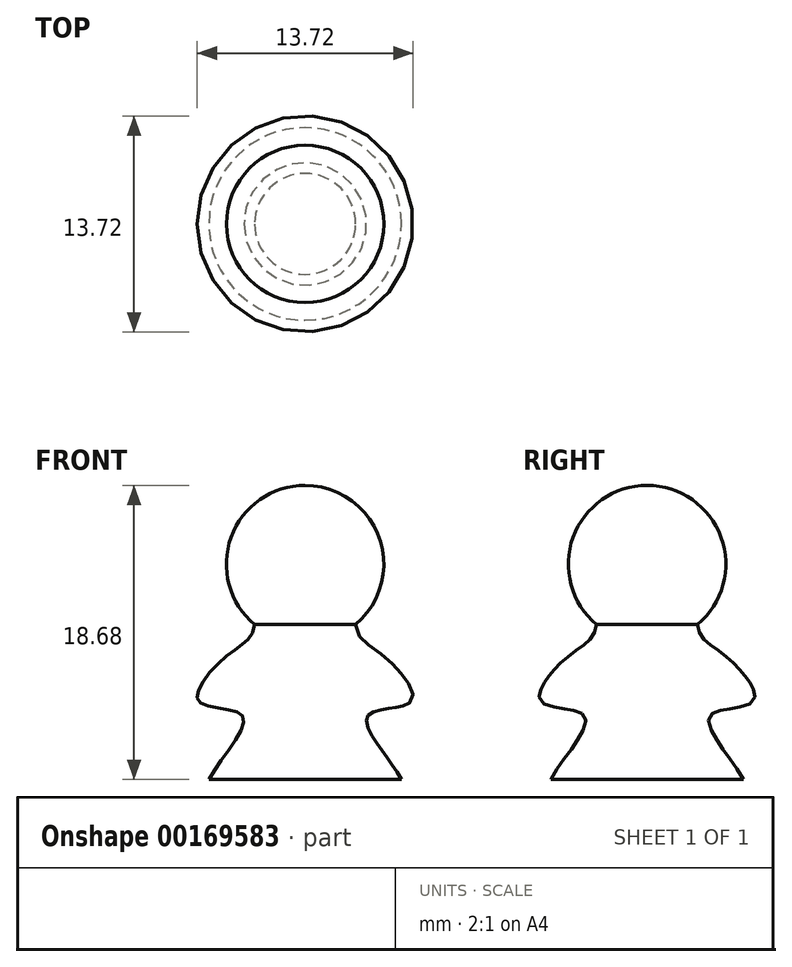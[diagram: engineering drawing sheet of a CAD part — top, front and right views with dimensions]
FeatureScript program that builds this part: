
annotation { "Feature Type Name" : "Feature", "Feature Type Description" : "" }
export const myFeature = defineFeature(function(context is Context, id is Id, definition is map)
    precondition{}
    {
        {
            var Q0;
            Q0=qCreatedBy(makeId("Front.planeOp"),FACE);
            var sketch = newSketch(context, id + "F0", { "sketchPlane" : qUnion([Q0])});
            skArc(sketch, "E0", {"start": v(0, 28.33) * mm, "mid": v(-4.7, 25.03) * mm, "end": v(-3.2, 19.5) * mm});
            skFitSpline(sketch, "E1", {"points": [v(-3.2, 19.5) * mm, v(-4.97, 17.5) * mm, v(-6.76, 14.62) * mm, v(-4, 13.74) * mm, v(-5.64, 10.42) * mm, v(-7.13, 7.5) * mm, v(-8.32, 4.29) * mm, v(-9, 0) * mm, v(0, 0.33) * mm], "startDerivative": vector(-3.98, -30.23) * mm, "endDerivative": vector(155.66, 0) * mm});
            skPoint(sketch, "E2.MirrorCS.end.orphan", {"position": v(9, 0) * mm});
            skPoint(sketch, "E3.orphan", {"position": v(3.2, 19.5) * mm});
            skPoint(sketch, "E4.MirrorCS.start.orphan", {"position": v(0, 0) * mm});
            skPoint(sketch, "E5.orphan", {"position": v(0, 53.09) * mm});
            skLineSegment(sketch, "E6.trimOffspring", {"start": v(0, 0.33) * mm, "end": v(0, 0) * mm});
            skLineSegment(sketch, "E7", {"start": v(0, 28.33) * mm, "end": v(0, 9.65) * mm});
            skLineSegment(sketch, "E8", {"start": v(-6.12, 9.65) * mm, "end": v(0, 9.65) * mm});
            skSolve(sketch);
        }
        {
            var Q0;
            Q0=qCreatedBy(makeId("Front.planeOp"),FACE);
            var sketch = newSketch(context, id + "F1", { "sketchPlane" : qUnion([Q0])});
            skLineSegment(sketch, "E9", {"start": v(0, 0) * mm, "end": v(0, 48.35) * mm});
            skSolve(sketch);
        }
        {
            var Q0;
            Q0=makeQuery(id+"F0.imprint","IMPRINT",FACE,{"disambiguationData":[TD([[makeQuery(id+"F0.imprint","IMPRINT",EDGE,{"derivedFrom":sQuery(id+"F0.wireOp",EDGE,"E0")}),1.0]])]});
            var Q1;
            Q1=sQuery(id+"F1.wireOp",EDGE,"E9");
            revolve(context, id + "F2", {"entities" : qUnion([Q0]), "axis" : qUnion([Q1]), "revolveType" : RevolveType.FULL});
        }
    });
